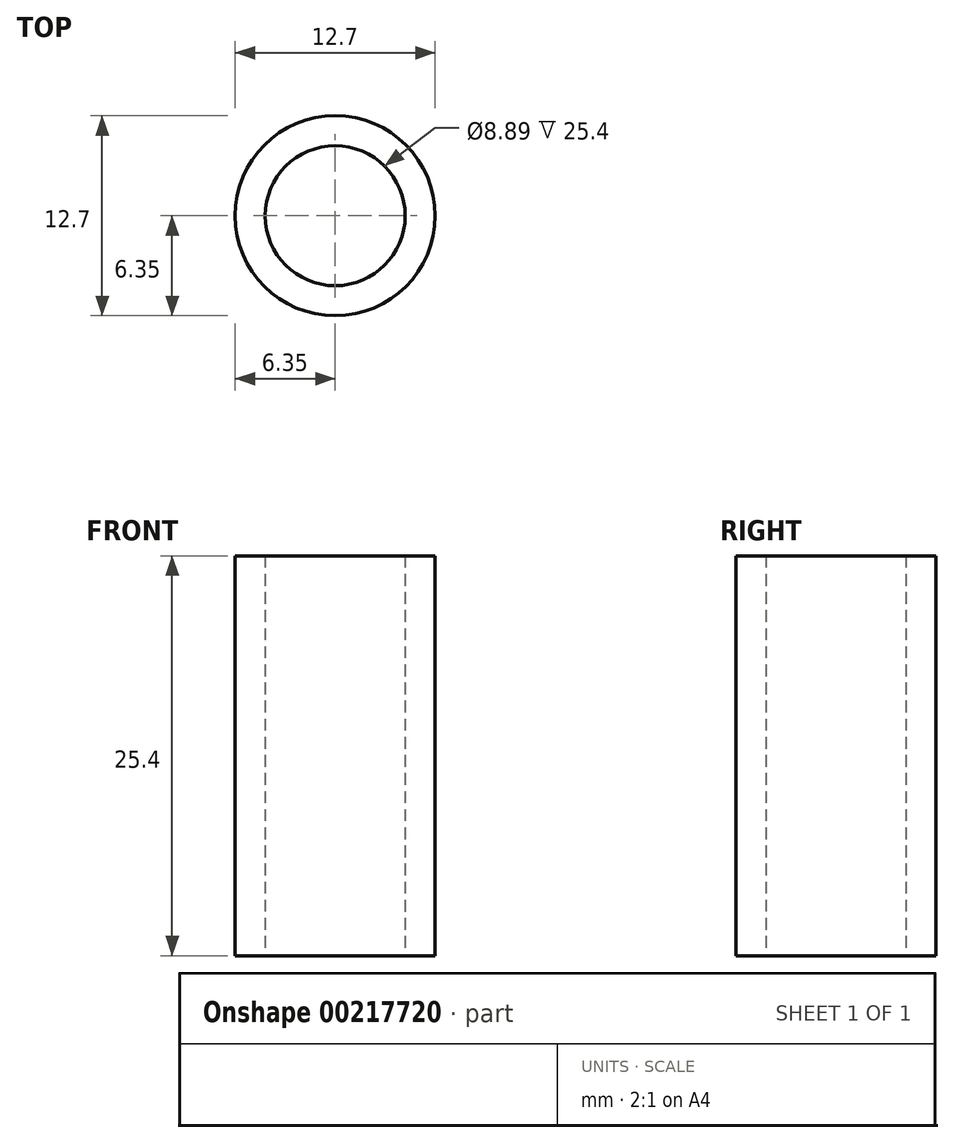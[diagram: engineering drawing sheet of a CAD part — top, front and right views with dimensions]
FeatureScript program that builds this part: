
annotation { "Feature Type Name" : "Feature", "Feature Type Description" : "" }
export const myFeature = defineFeature(function(context is Context, id is Id, definition is map)
    precondition{}
    {
        {
            var Q0;
            Q0=qCreatedBy(makeId("Top.planeOp"),FACE);
            var sketch = newSketch(context, id + "F0", { "sketchPlane" : qUnion([Q0])});
            skCircle(sketch, "E0", {"center": v(0, 0) * mm, "radius": 4.45 * mm});
            skCircle(sketch, "E1", {"center": v(0, 0) * mm, "radius": 6.35 * mm});
            skSolve(sketch);
        }
        {
            var Q0;
            Q0 = qSketchRegion(id + "F0", true);
            extrude(context, id + "F1", {"entities" : qUnion([Q0]), "depth" : 25.4 * mm, "offsetDistance" : 25.4 * mm});
        }
    });
